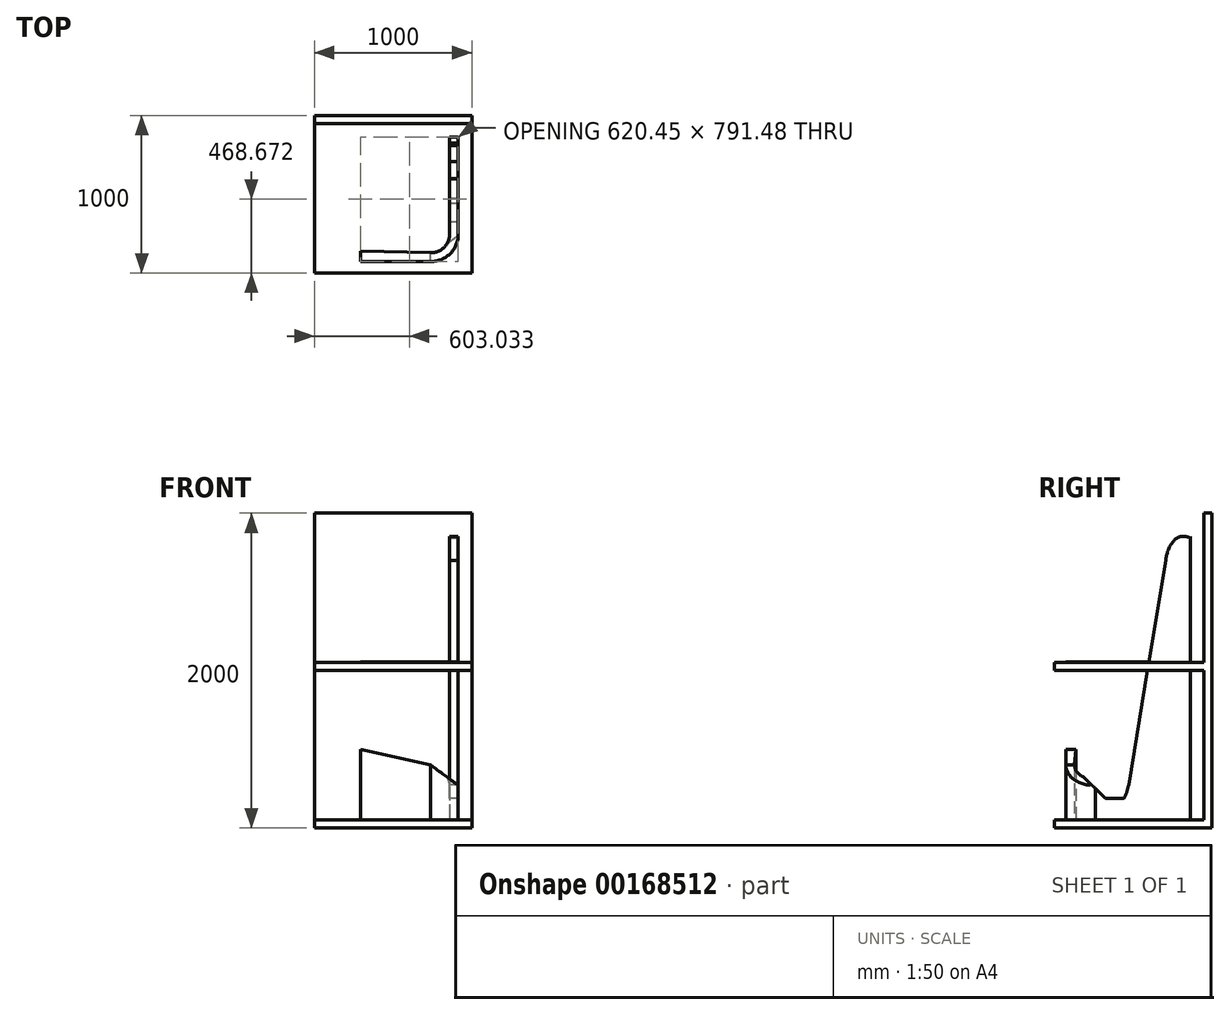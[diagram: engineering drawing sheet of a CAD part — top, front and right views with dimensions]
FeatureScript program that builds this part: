
annotation { "Feature Type Name" : "Feature", "Feature Type Description" : "" }
export const myFeature = defineFeature(function(context is Context, id is Id, definition is map)
    precondition{}
    {
        {
            var Q0;
            Q0=qCreatedBy(makeId("Right.planeOp"),FACE);
            var sketch = newSketch(context, id + "F0", { "sketchPlane" : qUnion([Q0])});
            skLineSegment(sketch, "E0", {"start": v(-503.73, -51.9) * mm, "end": v(496.27, -51.9) * mm});
            skLineSegment(sketch, "E1", {"start": v(496.27, -51.9) * mm, "end": v(496.27, 1948.1) * mm});
            skLineSegment(sketch, "E2", {"start": v(-503.73, -51.9) * mm, "end": v(-503.73, -1.1) * mm});
            skLineSegment(sketch, "E3", {"start": v(496.27, 1948.1) * mm, "end": v(445.47, 1948.1) * mm});
            skLineSegment(sketch, "E4", {"start": v(445.47, 1948.1) * mm, "end": v(445.47, 0) * mm});
            skLineSegment(sketch, "E5", {"start": v(445.47, 0) * mm, "end": v(-503.73, -1.1) * mm});
            skLineSegment(sketch, "E6", {"start": v(496.27, -51.9) * mm, "end": v(496.27, 948.1) * mm});
            skLineSegment(sketch, "E7", {"start": v(496.27, 948.1) * mm, "end": v(-503.73, 948.1) * mm});
            skLineSegment(sketch, "E8", {"start": v(-503.73, 948.1) * mm, "end": v(-503.73, 998.9) * mm});
            skLineSegment(sketch, "E9", {"start": v(-503.73, 998.9) * mm, "end": v(496.27, 998.9) * mm});
            skSolve(sketch);
        }
        {
            var Q0;
            {var subQ5=sQuery(id+"F0.wireOp",EDGE,"E8");Q0=makeQuery(id+"F0.imprint","IMPRINT",FACE,{"disambiguationData":[TD([[makeQuery(id+"F0.imprint","IMPRINT",EDGE,{"derivedFrom":subQ5}),-1.0]])]});}
            var Q1;
            {var subQ3=sQuery(id+"F0.wireOp",EDGE,"E9");var subQ5=sQuery(id+"F0.wireOp",EDGE,"E4");var subQ6=makeQuery(id+"F0.imprint","INTERSECT",VERTEX,{"derivedFrom":[subQ5,subQ3]});Q1=makeQuery(id+"F0.imprint","IMPRINT",FACE,{"disambiguationData":[TD([[makeQuery(id+"F0.imprint","IMPRINT",EDGE,{"disambiguationData":[TD([[subQ6,-1.0]])],"derivedFrom":subQ5}),1.0]])]});}
            var Q2;
            {var subQ0=sQuery(id+"F0.wireOp",EDGE,"E3");Q2=makeQuery(id+"F0.imprint","IMPRINT",FACE,{"disambiguationData":[TD([[makeQuery(id+"F0.imprint","IMPRINT",EDGE,{"derivedFrom":subQ0}),1.0]])]});}
            var Q3;
            Q3=makeQuery(id+"F0.imprint","IMPRINT",FACE,{"disambiguationData":[TD([[makeQuery(id+"F0.imprint","IMPRINT",EDGE,{"derivedFrom":sQuery(id+"F0.wireOp",EDGE,"E0")}),1.0]])]});
            extrude(context, id + "F1", {"entities" : qUnion([Q0, Q1, Q2, Q3]), "depth" : 1000 * mm});
        }
        {
            var Q0;
            Q0=qCreatedBy(makeId("Top.planeOp"),FACE);
            var sketch = newSketch(context, id + "F2", { "sketchPlane" : qUnion([Q0])});
            skLineSegment(sketch, "E10", {"start": v(292.8, -430.8) * mm, "end": v(738.26, -430.8) * mm});
            skCircle(sketch, "E11", {"center": v(740.8, -257.79) * mm, "radius": 173.03 * mm});
            skPoint(sketch, "E11.second.point", {"position": v(738.26, -84.77) * mm});
            skPoint(sketch, "E11.third.point", {"position": v(913.26, -243.86) * mm});
            skLineSegment(sketch, "E12", {"start": v(913.26, -243.86) * mm, "end": v(913.26, 360.68) * mm});
            skLineSegment(sketch, "E13", {"start": v(913.26, 360.68) * mm, "end": v(857.58, 360.68) * mm});
            skLineSegment(sketch, "E14", {"start": v(857.58, 360.68) * mm, "end": v(857.58, -243.86) * mm});
            skCircle(sketch, "E15", {"center": v(740.8, -257.79) * mm, "radius": 117.61 * mm});
            skLineSegment(sketch, "E16", {"start": v(738.26, -375.37) * mm, "end": v(292.8, -365.78) * mm});
            skLineSegment(sketch, "E17", {"start": v(292.8, -365.78) * mm, "end": v(292.8, -430.8) * mm});
            skSolve(sketch);
        }
        {
            var Q0;
            {var subQ0=sQuery(id+"F2.wireOp",EDGE,"E12");Q0=makeQuery(id+"F2.imprint","IMPRINT",FACE,{"disambiguationData":[TD([[makeQuery(id+"F2.imprint","IMPRINT",EDGE,{"derivedFrom":subQ0}),1.0]])]});}
            var Q1;
            {var subQ0=sQuery(id+"F2.wireOp",EDGE,"E11");var subQ2=makeQuery(id+"F2.imprint","INTERSECT",VERTEX,{"derivedFrom":[subQ0,sQuery(id+"F2.wireOp",EDGE,"E12")]});Q1=makeQuery(id+"F2.imprint","IMPRINT",FACE,{"disambiguationData":[TD([[makeQuery(id+"F2.imprint","IMPRINT",EDGE,{"disambiguationData":[TD([[subQ2,-1.0]])],"derivedFrom":subQ0}),1.0]])]});}
            var Q2;
            {var subQ0=sQuery(id+"F2.wireOp",EDGE,"E10");Q2=makeQuery(id+"F2.imprint","IMPRINT",FACE,{"disambiguationData":[TD([[makeQuery(id+"F2.imprint","IMPRINT",EDGE,{"derivedFrom":subQ0}),1.0]])]});}
            extrude(context, id + "F3", {"entities" : qUnion([Q0, Q1, Q2]), "operationType" : NewBodyOperationType.ADD, "depth" : 1800 * mm});
        }
        {
            var Q0;
            Q0=qCreatedBy(makeId("Right.planeOp"),FACE);
            var sketch = newSketch(context, id + "F4", { "sketchPlane" : qUnion([Q0])});
            skLineSegment(sketch, "E18", {"start": v(-436.84, 445.9) * mm, "end": v(-243.51, 445.9) * mm});
            skLineSegment(sketch, "E19", {"start": v(-243.51, 445.9) * mm, "end": v(-243.51, 220.35) * mm});
            skFitSpline(sketch, "E20", {"points": [v(-243.51, 220.35) * mm, v(-179.07, 134.43) * mm, v(-82.4, 118.32) * mm, v(-32.14, 220.35) * mm], "startDerivative": vector(152.3, -289.78) * mm, "endDerivative": vector(95.34, 377.42) * mm});
            skLineSegment(sketch, "E21", {"start": v(-32.14, 220.35) * mm, "end": v(202.95, 1646.4) * mm});
            skFitSpline(sketch, "E22", {"points": [v(202.95, 1646.4) * mm, v(209.4, 1682.89) * mm, v(228.57, 1735.1) * mm, v(257.88, 1774.53) * mm, v(282.39, 1794.77) * mm, v(318.62, 1800.1) * mm, v(350.58, 1793.7) * mm, v(360.17, 1786.25) * mm], "startDerivative": vector(33.27, 235.6) * mm, "endDerivative": vector(91.57, -94.36) * mm});
            skLineSegment(sketch, "E23", {"start": v(360.17, 1786.25) * mm, "end": v(360.17, 1808.16) * mm});
            skLineSegment(sketch, "E24", {"start": v(360.17, 1808.16) * mm, "end": v(-435.66, 1808.16) * mm});
            skLineSegment(sketch, "E25", {"start": v(-435.66, 1808.16) * mm, "end": v(-436.84, 445.9) * mm});
            skLineSegment(sketch, "E26", {"start": v(-436.36, 1002.89) * mm, "end": v(96.87, 1002.89) * mm});
            skLineSegment(sketch, "E27", {"start": v(96.87, 1002.89) * mm, "end": v(87.76, 947.63) * mm});
            skLineSegment(sketch, "E28", {"start": v(87.76, 947.63) * mm, "end": v(-436.4, 948.08) * mm});
            skLineSegment(sketch, "E29", {"start": v(-436.4, 948.08) * mm, "end": v(-436.36, 1002.89) * mm});
            skLineSegment(sketch, "E30", {"start": v(-179.07, 134.43) * mm, "end": v(-436.84, 134.43) * mm});
            skLineSegment(sketch, "E31", {"start": v(-436.84, 134.43) * mm, "end": v(221.35, 134.43) * mm});
            skLineSegment(sketch, "E32", {"start": v(-179.07, 134.43) * mm, "end": v(-348.02, 302.02) * mm});
            skLineSegment(sketch, "E33", {"start": v(-348.02, 302.02) * mm, "end": v(-348.02, 445.9) * mm});
            skSolve(sketch);
        }
        {
            var Q0;
            {var subQ1=sQuery(id+"F4.wireOp",EDGE,"E22");Q0=makeQuery(id+"F4.imprint","IMPRINT",FACE,{"disambiguationData":[TD([[makeQuery(id+"F4.imprint","IMPRINT",EDGE,{"derivedFrom":subQ1}),1.0]])]});}
            var Q1;
            {var subQ3=sQuery(id+"F4.wireOp",EDGE,"E18");Q1=makeQuery(id+"F4.imprint","IMPRINT",FACE,{"disambiguationData":[TD([[makeQuery(id+"F4.imprint","IMPRINT",EDGE,{"derivedFrom":subQ3}),1.0]])]});}
            var Q2;
            {var subQ0=sQuery(id+"F4.wireOp",EDGE,"E19");Q2=makeQuery(id+"F4.imprint","IMPRINT",FACE,{"disambiguationData":[TD([[makeQuery(id+"F4.imprint","IMPRINT",EDGE,{"derivedFrom":subQ0}),-1.0]])]});}
            extrude(context, id + "F5", {"entities" : qUnion([Q0, Q1, Q2]), "operationType" : NewBodyOperationType.REMOVE, "depth" : 5360 * mm});
        }
        {
            var Q0;
            Q0=qCreatedBy(makeId("Front.planeOp"),FACE);
            var sketch = newSketch(context, id + "F6", { "sketchPlane" : qUnion([Q0])});
            skLineSegment(sketch, "E34", {"start": v(293.01, 445.72) * mm, "end": v(737.58, 347.76) * mm});
            skLineSegment(sketch, "E35", {"start": v(737.58, 347.76) * mm, "end": v(669.26, 219.5) * mm});
            skLineSegment(sketch, "E36", {"start": v(669.26, 219.5) * mm, "end": v(912.65, 219.5) * mm});
            skLineSegment(sketch, "E37", {"start": v(912.65, 219.5) * mm, "end": v(737.58, 347.76) * mm});
            skLineSegment(sketch, "E38", {"start": v(912.65, 219.5) * mm, "end": v(912.65, 459.74) * mm});
            skLineSegment(sketch, "E39", {"start": v(912.65, 459.74) * mm, "end": v(293.01, 459.74) * mm});
            skLineSegment(sketch, "E40", {"start": v(293.01, 459.74) * mm, "end": v(293.01, 445.72) * mm});
            skSolve(sketch);
        }
        {
            var Q0;
            Q0=makeQuery(id+"F6.imprint","IMPRINT",FACE,{"disambiguationData":[TD([[makeQuery(id+"F6.imprint","IMPRINT",EDGE,{"derivedFrom":sQuery(id+"F6.wireOp",EDGE,"E34")}),1.0]])]});
            extrude(context, id + "F7", {"entities" : qUnion([Q0]), "operationType" : NewBodyOperationType.REMOVE, "depth" : 760 * mm, "hasSecondDirection" : true, "secondDirectionOppositeDirection" : false, "secondDirectionDepth" : 131 * mm});
        }
    });
